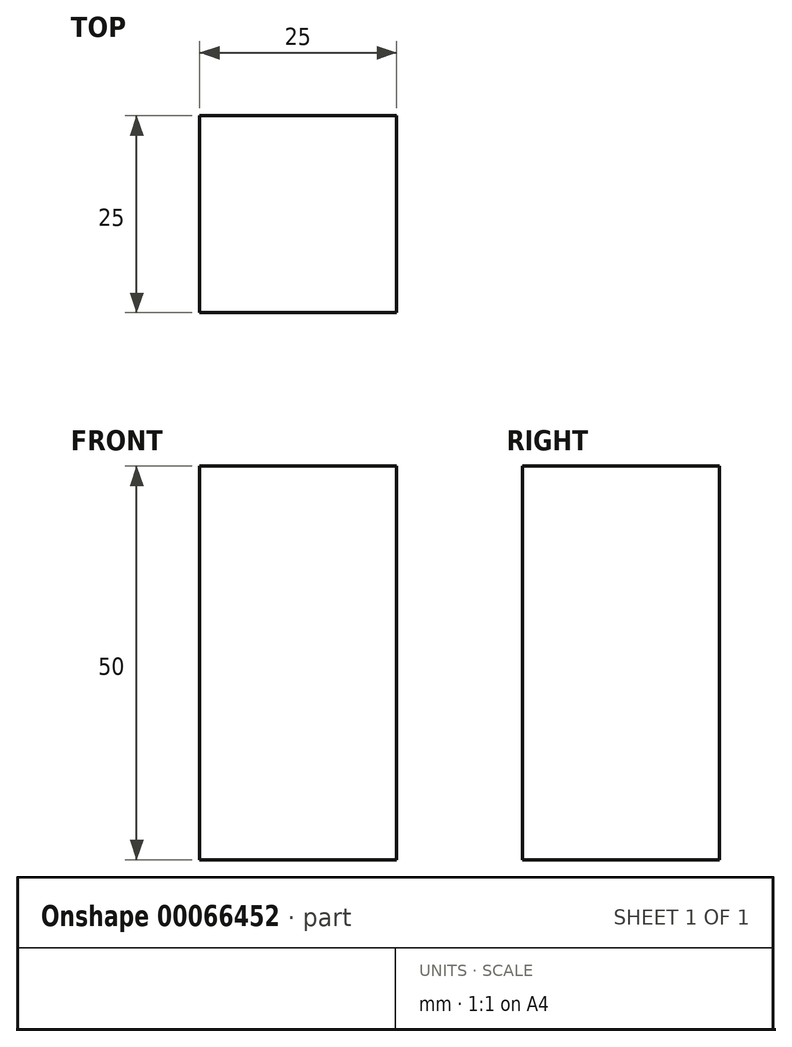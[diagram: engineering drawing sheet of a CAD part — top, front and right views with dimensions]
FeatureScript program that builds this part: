
annotation { "Feature Type Name" : "Feature", "Feature Type Description" : "" }
export const myFeature = defineFeature(function(context is Context, id is Id, definition is map)
    precondition{}
    {
        {
            var Q0;
            Q0=qCreatedBy(makeId("Front.planeOp"),FACE);
            var sketch = newSketch(context, id + "F0", { "sketchPlane" : qUnion([Q0])});
            skLineSegment(sketch, "E0.rect.bottom", {"start": v(12.5, 25) * mm, "end": v(-12.5, 25) * mm});
            skLineSegment(sketch, "E0.rect.top", {"start": v(12.5, -25) * mm, "end": v(-12.5, -25) * mm});
            skLineSegment(sketch, "E0.rect.left", {"start": v(12.5, 25) * mm, "end": v(12.5, -25) * mm});
            skLineSegment(sketch, "E0.rect.right", {"start": v(-12.5, 25) * mm, "end": v(-12.5, -25) * mm});
            skPoint(sketch, "E0.rect.middle", {"position": v(0, 0) * mm});
            skSolve(sketch);
        }
        {
            var Q0;
            Q0 = qSketchRegion(id + "FVcTSvgTbZXjwMy_0", true);
            var Q1;
            Q1 = qSketchRegion(id + "F0", true);
            extrude(context, id + "F1", {"entities" : qUnion([Q0, Q1]), "depth" : 25 * mm});
        }
        {
            var Q0;
            Q0=qCreatedBy(makeId("Front.planeOp"),FACE);
            var sketch = newSketch(context, id + "F2", { "sketchPlane" : qUnion([Q0])});
            skLineSegment(sketch, "E1.rect.bottom", {"start": v(100.06, 22.71) * mm, "end": v(-100.06, 22.71) * mm});
            skLineSegment(sketch, "E1.rect.top", {"start": v(100.06, -22.71) * mm, "end": v(-100.06, -22.71) * mm});
            skLineSegment(sketch, "E1.rect.left", {"start": v(100.06, 22.71) * mm, "end": v(100.06, -22.71) * mm});
            skLineSegment(sketch, "E1.rect.right", {"start": v(-100.06, 22.71) * mm, "end": v(-100.06, -22.71) * mm});
            skPoint(sketch, "E1.rect.middle", {"position": v(0, 0) * mm});
            skLineSegment(sketch, "E2.rect.bottom", {"start": v(84.8, 42.31) * mm, "end": v(115.32, 42.31) * mm});
            skLineSegment(sketch, "E2.rect.top", {"start": v(84.8, 3.11) * mm, "end": v(115.32, 3.11) * mm});
            skLineSegment(sketch, "E2.rect.left", {"start": v(84.8, 42.31) * mm, "end": v(84.8, 3.11) * mm});
            skLineSegment(sketch, "E2.rect.right", {"start": v(115.32, 42.31) * mm, "end": v(115.32, 3.11) * mm});
            skPoint(sketch, "E2.rect.middle", {"position": v(100.06, 22.71) * mm});
            skLineSegment(sketch, "E3.rect.bottom", {"start": v(60.5, 52.78) * mm, "end": v(145.12, 52.78) * mm});
            skLineSegment(sketch, "E3.rect.top", {"start": v(60.5, 32.68) * mm, "end": v(145.12, 32.68) * mm});
            skLineSegment(sketch, "E3.rect.left", {"start": v(60.5, 52.78) * mm, "end": v(60.5, 32.68) * mm});
            skLineSegment(sketch, "E3.rect.right", {"start": v(145.12, 52.78) * mm, "end": v(145.12, 32.68) * mm});
            skPoint(sketch, "E3.rect.middle", {"position": v(102.81, 42.73) * mm});
            skLineSegment(sketch, "E4.rect.bottom", {"start": v(145.15, 45.42) * mm, "end": v(130.67, 45.42) * mm});
            skLineSegment(sketch, "E4.rect.top", {"start": v(145.15, 49.37) * mm, "end": v(130.67, 49.37) * mm});
            skLineSegment(sketch, "E4.rect.left", {"start": v(145.15, 45.42) * mm, "end": v(145.15, 49.37) * mm});
            skLineSegment(sketch, "E4.rect.right", {"start": v(130.67, 45.42) * mm, "end": v(130.67, 49.37) * mm});
            skPoint(sketch, "E4.rect.middle", {"position": v(137.91, 47.4) * mm});
            skSolve(sketch);
        }
        {
            var Q0;
            Q0=makeQuery(id+"F0.imprint","IMPRINT",FACE,{"disambiguationData":[TD([[makeQuery(id+"F0.imprint","IMPRINT",EDGE,{"derivedFrom":sQuery(id+"F0.wireOp",EDGE,"E0.rect.bottom")}),1.0]])]});
            extrude(context, id + "F3", {"entities" : qUnion([Q0]), "operationType" : NewBodyOperationType.ADD, "depth" : 10 * mm});
        }
    });
